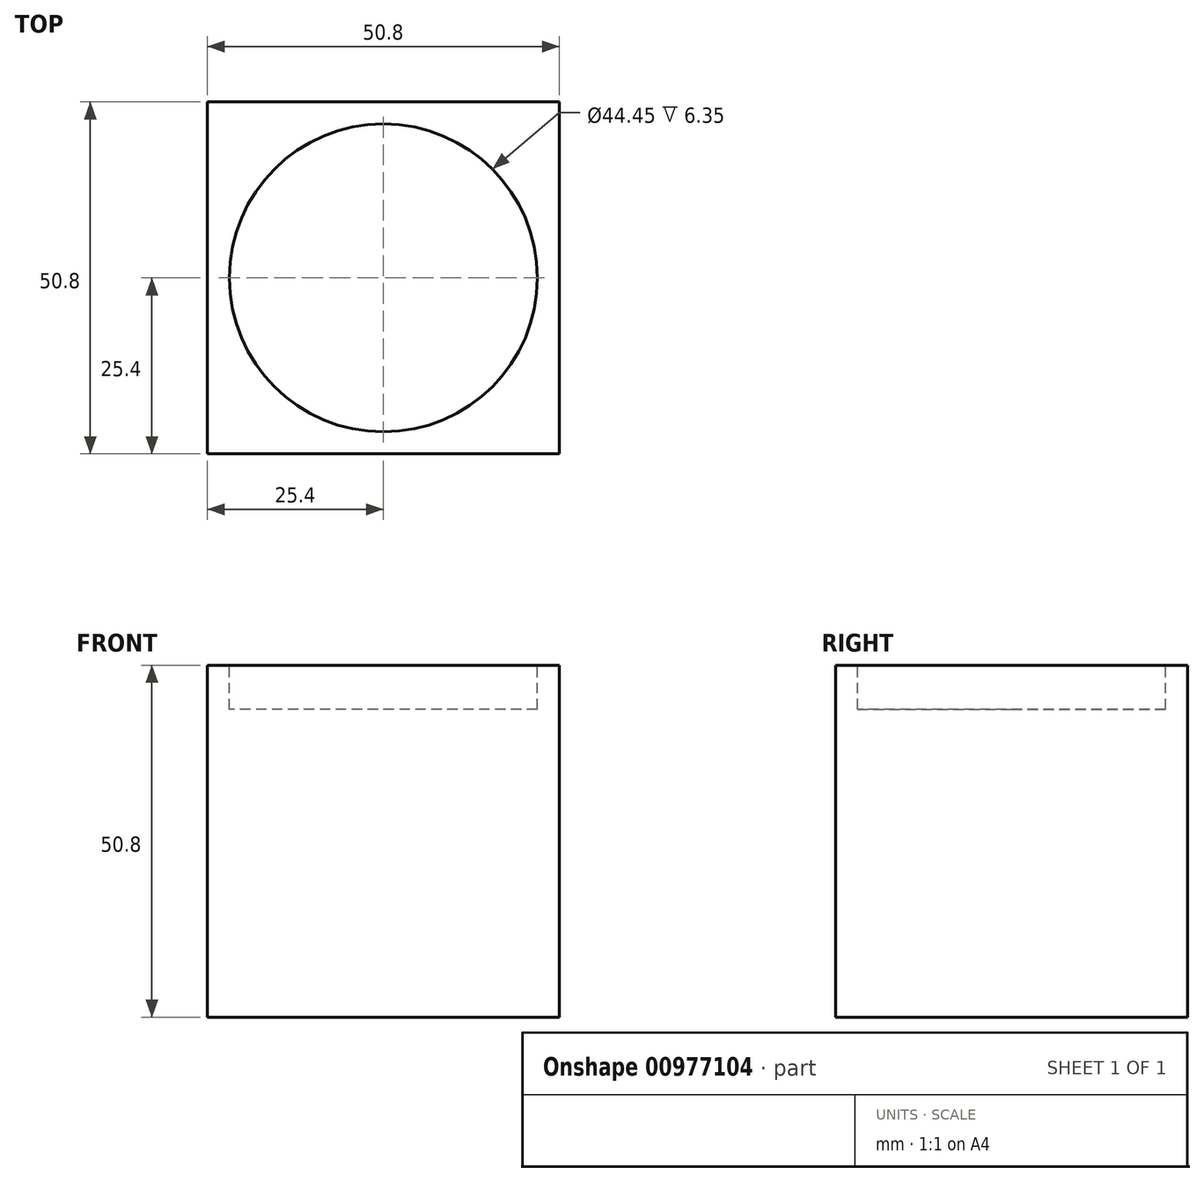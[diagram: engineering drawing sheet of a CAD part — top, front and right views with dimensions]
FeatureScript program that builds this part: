
annotation { "Feature Type Name" : "Feature", "Feature Type Description" : "" }
export const myFeature = defineFeature(function(context is Context, id is Id, definition is map)
    precondition{}
    {
        {
            var Q0;
            Q0=qCreatedBy(makeId("Top.planeOp"),FACE);
            var sketch = newSketch(context, id + "F0", { "sketchPlane" : qUnion([Q0])});
            skLineSegment(sketch, "E0.bottom", {"start": v(0, 0) * mm, "end": v(-50.8, 0) * mm});
            skLineSegment(sketch, "E0.top", {"start": v(0, -50.8) * mm, "end": v(-50.8, -50.8) * mm});
            skLineSegment(sketch, "E0.left", {"start": v(0, 0) * mm, "end": v(0, -50.8) * mm});
            skLineSegment(sketch, "E0.right", {"start": v(-50.8, 0) * mm, "end": v(-50.8, -50.8) * mm});
            skSolve(sketch);
        }
        {
            var Q0;
            Q0 = qSketchRegion(id + "F0", true);
            extrude(context, id + "F1", {"entities" : qUnion([Q0]), "depth" : 50.8 * mm, "offsetDistance" : 25.4 * mm});
        }
        {
            var Q0;
            Q0=makeQuery(id+"F1.opExtrude","CAP_FACE",FACE,{"disambiguationData":[OSD([sQuery(id+"F0.wireOp",EDGE,"E0.bottom"),sQuery(id+"F0.wireOp",EDGE,"E0.top"),sQuery(id+"F0.wireOp",EDGE,"E0.left"),sQuery(id+"F0.wireOp",EDGE,"E0.right")])],"isStart":false});
            var sketch = newSketch(context, id + "F2", { "sketchPlane" : qUnion([Q0])});
            skCircle(sketch, "E1", {"center": v(-25.4, -25.4) * mm, "radius": 22.23 * mm});
            skLineSegment(sketch, "E2", {"start": v(-50.8, 0) * mm, "end": v(0, -50.8) * mm});
            skSolve(sketch);
        }
        {
            var Q0;
            Q0 = qSketchRegion(id + "F2", true);
            extrude(context, id + "F3", {"entities" : qUnion([Q0]), "operationType" : NewBodyOperationType.REMOVE, "oppositeDirection" : true, "depth" : 6.35 * mm, "offsetDistance" : 25.4 * mm});
        }
    });
